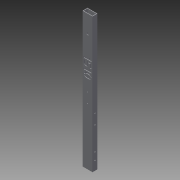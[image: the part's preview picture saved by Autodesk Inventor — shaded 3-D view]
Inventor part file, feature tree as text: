
AUTODESK INVENTOR PART (.ipt)
format: ipt  version: 2013 (Build 170138000, 138)  size: 250,368 bytes
history: native  units: in
note: dims shown in document units (in); Inventor stores cm internally (conversion verified against a paired STEP export)
features: sketch x8, extrude x7, hole x1
ambient origin geometry x8: Origin, YZ Plane, XZ Plane, XY Plane, X Axis, Y Axis, Z Axis, Center Point
bodies: Solid1 (feature_tree)
feature tree (16):
  extrude  "Extrusion1"  Depth=1.0in
  extrude  "Extrusion2"  Depth=0.75in
  extrude  "Extrusion4"  Depth=1.0in
  extrude  "Extrusion6"  Depth=0.5in
  extrude  "Extrusion9"  Depth=0.5in TaperAngle=0.0deg
  hole  "Hole1"  [1 undecoded]
  extrude  "Extrusion10"  Depth=2.0in
  extrude  "Extrusion11"  Depth=0.25in
  sketch  "Sketch1"  dims[d0=2.0in d1=1.0in]
  sketch  "Sketch2"  dims[d2=1.75in d3=0.75in]
  sketch  "Sketch4"  dims[d4=24.0in d5=0.0in d6=1.0in]
  sketch  "Sketch6"  dims[d7=1.0in d8=0.5in]
  sketch  "Sketch8"  dims[d9=24.0in d10=0.0in d25=0.5in d26=0.0in]
  sketch  "Sketch9"  dims[d35=2.5in d36=0.0in d49=13.543in]
  sketch  "Sketch10"  dims[d50=90.0deg d51=2.0in]
  sketch  "Sketch11"  dims[d52=180.0deg d53=0.25in d54=0.25in d55=2.0in d56=0.0in d57=3.313in d58=1.5in d59=90.0deg d60=0.25in d61=0.75in d62=0.375in d63=0.25in d64=0.5635in d65=1.0in d66=0.8108in d67=0.5in d68=90.0deg d69=3.75in d75=0.25in d76=150.0deg d77=0.25in d78=0.25in d79=1.0in d80=0.875in d81=0.25in d82=0.625in d83=0.25in d87=45.0deg d88=0.442in d89=135.0deg d90=0.442in d95=1.5in d96=0.25in d97=0.5in d98=150.0deg d103=135.0deg d105=135.0deg d107=45.0deg d109=45.0deg d114=0.5in d115=0.5in d118=0.0625in d119=0.25in d120=0.25in d121=0.25in d122=0.25in d123=0.5in d124=0.5in d125=0.5in d126=0.5in d127=0.5in d128=0.25in d129=1.0in d130=0.25in d131=0.0in d132=17.0in d133=90.0deg d134=2.0in d135=180.0deg d136=0.25in d137=0.25in d138=2.0in d139=0.0in]
note: 1 required parameter value undecoded (feature->parameter linkage not recoverable at this tier; creation-order binding heuristic only, values carry confidence <= 0.55)
